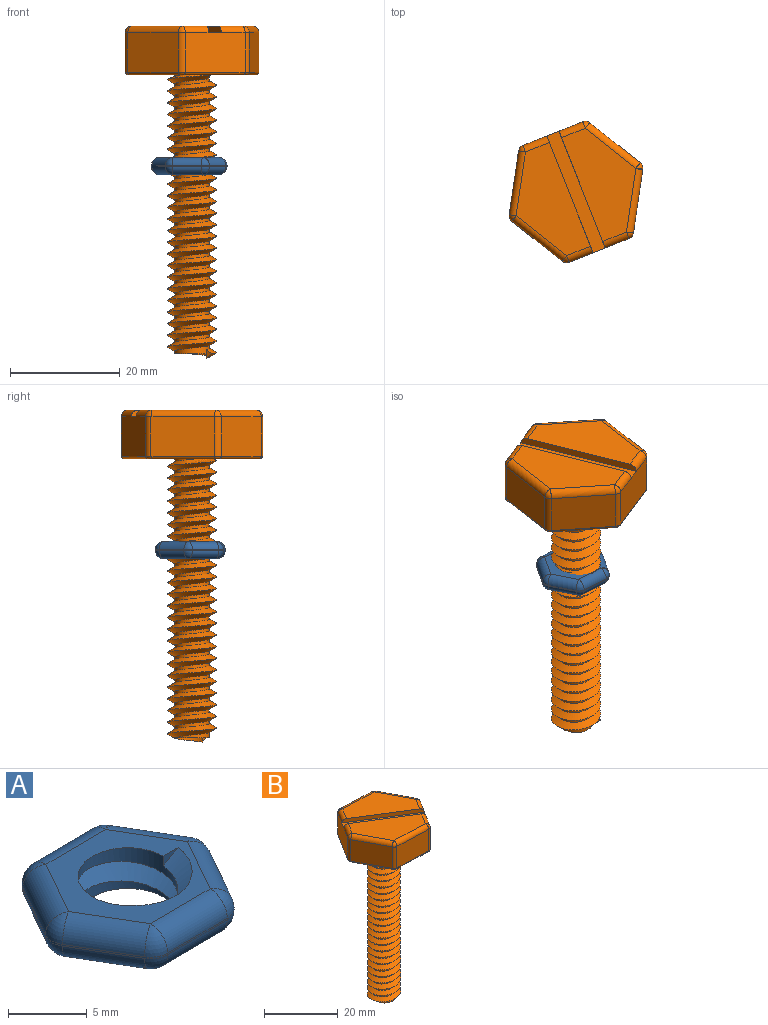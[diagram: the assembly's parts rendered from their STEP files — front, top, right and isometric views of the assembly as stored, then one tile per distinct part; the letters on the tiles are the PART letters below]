
ASSEMBLY  parts=2 mates=1
PART A: 43 faces, bbox 14.6x13.2x5.5 mm
  f0: plane 11.53x10.14mm, normal (0,0,1), area 38.2mm2, adj f6,f15,f16,f25,f26,f34,f35,f39
  f1: plane 5.38x0.13mm, normal (0.01,-1,0), area 0.7mm2, adj f27,f32,f35,f38
  f2: plane 4.64x2.73mm, normal (-0.86,-0.51,0), area 0.7mm2, adj f24,f33,f34,f38
  f3: plane 4.68x2.65mm, normal (-0.87,0.49,0), area 0.7mm2, adj f14,f23,f24,f25
  f4: plane 5.38x0.13mm, normal (-0.01,1,0), area 0.7mm2, adj f9,f13,f14,f15
  f5: plane 4.64x2.73mm, normal (0.86,0.51,0), area 0.7mm2, adj f9,f12,f16,f17
  f6: cylinder r=3.17mm len=6.35mm, axis (0,0,1), area 23.2mm2, adj f0,f8,f39,f40,f41,f42
  f7: plane 4.68x2.65mm, normal (0.87,-0.49,0), area 0.7mm2, adj f17,f22,f26,f27
  f8: plane 11.53x10.14mm, normal (0,0,-1), area 38.2mm2, adj f6,f12,f13,f22,f23,f32,f33,f41
  f9: cylinder r=1.52mm len=1.33mm, axis (0,0,1), area 0.2mm2, adj f4,f5,f10,f11
  f10: sphere r=1.52mm, area 2.4mm2, adj f9,f12,f13
  f11: sphere r=1.52mm, area 2.9mm2, adj f9,f15,f16
  f12: cylinder r=1.52mm len=5.41mm, axis (-0.51,0.86,0), area 12.9mm2, adj f5,f8,f10,f18
  f13: cylinder r=1.52mm len=5.4mm, axis (-1,-0.01,0), area 12.9mm2, adj f4,f8,f10,f19
  f14: cylinder r=1.52mm len=1.31mm, axis (0,0,1), area 0.2mm2, adj f3,f4,f19,f20
  f15: cylinder r=1.52mm len=5.4mm, axis (1,0.01,0), area 12.9mm2, adj f0,f4,f11,f20
  f16: cylinder r=1.52mm len=5.41mm, axis (0.51,-0.86,0), area 12.9mm2, adj f0,f5,f11,f21
  f17: cylinder r=1.52mm len=1.52mm, axis (0,0,1), area 0.2mm2, adj f5,f7,f18,f21
  f18: sphere r=1.52mm, area 2.4mm2, adj f12,f17,f22
  f19: sphere r=1.52mm, area 2.4mm2, adj f13,f14,f23
  f20: sphere r=1.52mm, area 2.4mm2, adj f14,f15,f25
  f21: sphere r=1.52mm, area 2.4mm2, adj f16,f17,f26
  f22: cylinder r=1.52mm len=5.44mm, axis (0.49,0.87,0), area 12.9mm2, adj f7,f8,f18,f28
  f23: cylinder r=1.52mm len=5.44mm, axis (-0.49,-0.87,0), area 12.9mm2, adj f3,f8,f19,f29
  f24: cylinder r=1.52mm len=1.52mm, axis (0,0,1), area 0.2mm2, adj f2,f3,f29,f30
  f25: cylinder r=1.52mm len=5.44mm, axis (0.49,0.87,0), area 12.9mm2, adj f0,f3,f20,f30
  f26: cylinder r=1.52mm len=5.44mm, axis (-0.49,-0.87,0), area 12.9mm2, adj f0,f7,f21,f31
  f27: cylinder r=1.52mm len=1.31mm, axis (0,0,1), area 0.2mm2, adj f1,f7,f28,f31
  f28: sphere r=1.52mm, area 2.4mm2, adj f22,f27,f32
  f29: sphere r=1.52mm, area 2.4mm2, adj f23,f24,f33
  f30: sphere r=1.52mm, area 2.4mm2, adj f24,f25,f34
  f31: sphere r=1.52mm, area 2.4mm2, adj f26,f27,f35
  f32: cylinder r=1.52mm len=5.4mm, axis (1,0.01,0), area 12.9mm2, adj f1,f8,f28,f36
  f33: cylinder r=1.52mm len=5.41mm, axis (0.51,-0.86,0), area 12.9mm2, adj f2,f8,f29,f36
  f34: cylinder r=1.52mm len=5.41mm, axis (-0.51,0.86,0), area 12.9mm2, adj f0,f2,f30,f37
  f35: cylinder r=1.52mm len=5.4mm, axis (-1,-0.01,0), area 12.9mm2, adj f0,f1,f31,f37
  f36: sphere r=1.52mm, area 2.9mm2, adj f32,f33,f38
  f37: sphere r=1.52mm, area 2.4mm2, adj f34,f35,f38
  f38: cylinder r=1.52mm len=1.33mm, axis (0,0,1), area 0.2mm2, adj f1,f2,f36,f37
  f39: bspline ~10.38x8.99mm, area 49mm2, adj f0,f6,f41,f42
  f40: plane 1.32x0.76mm, normal (0,-1,0), area 0.5mm2, adj f0,f6,f42
  f41: plane 1.32x0.76mm, normal (0,-1,0), area 0.5mm2, adj f6,f8,f39
  f42: bspline ~10.38x8.99mm, area 49mm2, adj f6,f8,f39,f40
PART B: 51 faces, bbox 27x24.2x61.2 mm
  f0: plane 19.7x14.75mm, normal (0,0,1), area 154.6mm2, adj f1,f2,f27,f32,f48
  f1: cylinder r=1.27mm len=4.64mm, axis (-0.53,-0.85,0), area 9.3mm2, adj f0,f14,f24,f48
  f2: cylinder r=1.27mm len=4.64mm, axis (0.53,0.85,0), area 9.3mm2, adj f0,f11,f34,f48
  f3: plane 1.32x0.76mm, normal (0,1,0), area 0.5mm2, adj f6,f9,f17
  f4: bspline ~51.56x10.38mm, area 880.4mm2, adj f6,f7,f9,f17
  f5: plane 6.35x6.35mm, normal (0,0,-1), area 31.7mm2, adj f6,f8
  f6: cylinder r=3.17mm len=50.8mm, axis (0,0,1), area 366.6mm2, adj f3,f4,f5,f7,f9,f17
  f7: plane 1.52x1.32mm, normal (0,-1,0), area 1mm2, adj f4,f6,f8,f9
  f8: cylinder r=3.17mm len=5.22mm, axis (0,0,-1), area 2.7mm2, adj f5,f7,f9
  f9: bspline ~51.56x10.38mm, area 884.7mm2, adj f3,f4,f6,f7,f8
  f10: plane 11.72x7.11mm, normal (0.04,1,0), area 83.4mm2, adj f26,f32,f35,f43
  f11: plane 9.94x7.11mm, normal (-0.85,0.53,0), area 83.4mm2, adj f2,f29,f33,f35,f47,f50
  f12: plane 10.36x7.11mm, normal (-0.88,-0.47,0), area 83.4mm2, adj f23,f28,f29,f44
  f13: plane 11.72x7.11mm, normal (-0.04,-1,0), area 83.4mm2, adj f18,f22,f23,f40
  f14: plane 9.94x7.11mm, normal (0.85,-0.53,0), area 83.4mm2, adj f1,f18,f20,f21,f36,f50
  f15: plane 10.36x7.11mm, normal (0.88,0.47,0), area 83.4mm2, adj f20,f26,f27,f39
  f16: plane 19.7x14.75mm, normal (0,0,1), area 154.6mm2, adj f21,f22,f28,f33,f49
  f17: plane 25.74x23.02mm, normal (0,0,-1), area 376mm2, adj f3,f4,f6,f36,f37,f38,f39,f40
  f18: cylinder r=1.27mm len=7.11mm, axis (0,0,-1), area 9.5mm2, adj f13,f14,f19,f38
  f19: sphere r=1.27mm, area 1.7mm2, adj f18,f21,f22
  f20: cylinder r=1.27mm len=7.11mm, axis (0,0,-1), area 9.5mm2, adj f14,f15,f24,f37
  f21: cylinder r=1.27mm len=4.64mm, axis (-0.53,-0.85,0), area 9.3mm2, adj f14,f16,f19,f49
  f22: cylinder r=1.27mm len=11.77mm, axis (-1,0.04,0), area 23.4mm2, adj f13,f16,f19,f25
  f23: cylinder r=1.27mm len=7.11mm, axis (0,0,-1), area 9.5mm2, adj f12,f13,f25,f42
  f24: sphere r=1.27mm, area 1.7mm2, adj f1,f20,f27
  f25: sphere r=1.27mm, area 1.7mm2, adj f22,f23,f28
  f26: cylinder r=1.27mm len=7.11mm, axis (0,0,-1), area 9.5mm2, adj f10,f15,f30,f41
  f27: cylinder r=1.27mm len=10.96mm, axis (0.47,-0.88,0), area 23.4mm2, adj f0,f15,f24,f30
  f28: cylinder r=1.27mm len=10.96mm, axis (-0.47,0.88,0), area 23.4mm2, adj f12,f16,f25,f31
  f29: cylinder r=1.27mm len=7.11mm, axis (0,0,-1), area 9.5mm2, adj f11,f12,f31,f46
  f30: sphere r=1.27mm, area 2mm2, adj f26,f27,f32
  f31: sphere r=1.27mm, area 1.7mm2, adj f28,f29,f33
  f32: cylinder r=1.27mm len=11.77mm, axis (1,-0.04,0), area 23.4mm2, adj f0,f10,f30,f34
  f33: cylinder r=1.27mm len=4.64mm, axis (0.53,0.85,0), area 9.3mm2, adj f11,f16,f31,f49
  f34: sphere r=1.27mm, area 1.7mm2, adj f2,f32,f35
  f35: cylinder r=1.27mm len=7.11mm, axis (0,0,-1), area 9.5mm2, adj f10,f11,f34,f45
  f36: cylinder r=0.51mm len=10.21mm, axis (0.53,0.85,0), area 9.4mm2, adj f14,f17,f37,f38
  f37: torus R=0.76mm, axis (0,0,1), area 0.9mm2, adj f17,f20,f36,f39
  f38: torus R=0.76mm, axis (0,0,1), area 0.9mm2, adj f17,f18,f36,f40
  f39: cylinder r=0.51mm len=10.6mm, axis (-0.47,0.88,0), area 9.4mm2, adj f15,f17,f37,f41
  f40: cylinder r=0.51mm len=11.74mm, axis (1,-0.04,0), area 9.4mm2, adj f13,f17,f38,f42
  f41: torus R=0.76mm, axis (0,0,1), area 0.9mm2, adj f17,f26,f39,f43
  f42: torus R=0.76mm, axis (0,0,1), area 0.9mm2, adj f17,f23,f40,f44
  f43: cylinder r=0.51mm len=11.74mm, axis (-1,0.04,0), area 9.4mm2, adj f10,f17,f41,f45
  f44: cylinder r=0.51mm len=10.6mm, axis (0.47,-0.88,0), area 9.4mm2, adj f12,f17,f42,f46
  f45: torus R=0.76mm, axis (0,0,1), area 0.9mm2, adj f17,f35,f43,f47
  f46: torus R=0.76mm, axis (0,0,1), area 0.9mm2, adj f17,f29,f44,f47
  f47: cylinder r=0.51mm len=10.21mm, axis (-0.53,-0.85,0), area 9.4mm2, adj f11,f17,f45,f46
  f48: plane 19.37x12.13mm, normal (-0.53,-0.85,0), area 28.3mm2, adj f0,f1,f2,f50
  f49: plane 19.37x12.13mm, normal (0.53,0.85,0), area 28.3mm2, adj f16,f21,f33,f50
  f50: plane 20.64x14.15mm, normal (0,0,1), area 54.4mm2, adj f11,f14,f48,f49
PLACE A rot(axis=(0.03,1,0),180deg) t=(9.46,-8.21,-45.66)mm
PLACE B rot(axis=(0,0,-1),36.3deg) t=(9.99,-8.52,23.36)mm fixed
MATE cylindrical A.f8 <-> B.f6  axis (0,0,1) through (9.99,-8.52,8.31)mm
